# Revit family: Construction_Other_Sjobergs_Bandsaw
name_source: partatom
category: Specialty Equipment
revit_build: Autodesk Revit 2017 (Build: 20190508_0315(x64)
units: mm (PartAtom-declared; Revit-internal decimal feet)

## family parameters
Always vertical = Yes
Cut with Voids When Loaded = No
OmniClass Number = 23.45.30.14.11
OmniClass Title = Commercial Dishwashers
Part Type = Normal
Room Calculation Point = No
Round Connector Dimension = Use Diameter
Shared = No
Work Plane-Based = No

## types (1)
- 37030 EJCA Bandsaw BS500
    AssetType = Movable
    BIMObjectName = Construction_Other_Sjobergs_Bandsaw
    BandsawSizes = Table size 630x550mm. Working height 980 mm. Total height 2000 mm.
    Brand = EJCA
    Category = Machinery & tools
    Color = Green
    ConvergoRefNr = 0184-2005-0021-SE
    Cost = 0 $
    CuttingSpeed = 21 (1260 m/min)
    Description = EJCA Band saw BS500 is the best band saw in the market. The right choice for those who have long life requirements. Everything is of the best quality. For example, the automatic brake that brakes softly and efficiently and that you never need to adjust, or that you can easily move the machine with a "hand truck" (recesses are already on the machine). The EJCA BS500 is the optimal band saw with the greatest emphasis on safety, environment and workability.
    DurationUnit = Year
    ElectricalDeviceNominalPower = 1500 W
    Features = Automatic brake that brakes softly and effectively and which you never have need to adjust, and that you can easily move the machine with a "hand truck" (recesses are already on the machine).The unique saw blade guide is top class with ground, hardened and ball bearing blade guide rollers around. The protection around the saw blade is optimal with a generous protection of aluminum profiles with telescopic function. The double table cradle is very sturdy and stable and can be tilted +45 degrees. The band saw blade voltage is read on a scale that helps you get the right voltage. EJCA Service guarantees that you never have to stand for any length of time with a band saw inoperative. CE standards.
    Finish = Cast iron
    HasProtectiveEarth = Yes
    IfcExportAs = NOTDEFINED
    IfcExportType = IfcElectricalDeviceCommon
    MachineryMainMaterial = Green metal
    MachineryQuaternaryMaterial = Clearance
    MachinerySecondaryMaterial = Black Metal
    MachineryTertiaryMaterial = Stainless Steel
    Manufacturer = Sjöbergs
    ManufacturerName = Sjöbergs
    ManufacturerURL = https://www.sjobergs.se
    Material = Metal, plastic
    MaximumSawDepth = 3900 mm
    MaximumSawHeight = 3940 mm
    MaximumSawbladeWidth = 3840 mm
    Model = 37030 EJCA Bandsaw BS500
    ModelReference = 37030
    NBSDescription = School art, design and technology tables and workbenches;
    NBSReference = 45-35-20/320
    Name = Sjobergs_Bandsaw
    NominalCurrent = 0 A
    NominalDepth = 590 mm  [stored 1.9357 ft]
    NominalFrequencyRange = 0 Hz
    NominalHeight = 2000 mm  [stored 6.56168 ft]
    NominalVoltage = 0 V
    NominalWidth = 870 mm  [stored 2.85433 ft]
    NumberOfPoles = 0
    PhaseAngle = 0.00°
    ProductDatasheet = https://www.sjobergs.se
    ProductInformation = EJCA Band saw BS500 is the best band saw in the market. The right choice for those who have long life requirements. Everything is of the best quality. For example, the automatic brake that brakes softly and efficiently and that you never need to adjust, or that you can easily move the machine with a "hand truck" (recesses are already on the machine). The EJCA BS500 is the optimal band saw with the greatest emphasis on safety, environment and workability.
    SawBladeLength = 370 mm
    SawBladeMaxLength = 500 mm
    SawBladeMinLength = 20 mm
    SawWheels = Ø 505 mm
    Shape = Sculptured
    Size = 870x590x2000 mm
    URL = https://www.sjobergs.se
    Uniclass2 = Pr_40_50_21
    Uniclass2015Description = Desks, Tables And Worktops
    Uniclass2015Reference = Pr_40_50_21_76
    UsageCurrent = 0 A
    Version = 1
    VersionDate = 01/07/2020
    WarrantyDurationUnit = Year
    Weight = 250.0 kg

note: [stored X ft] marks values corroborated as IEEE doubles in the binary element streams (Revit-internal decimal feet)

## geometry (parser evidence)
native form markers: Sweep x4
no freeform markers — native parametric forms only
